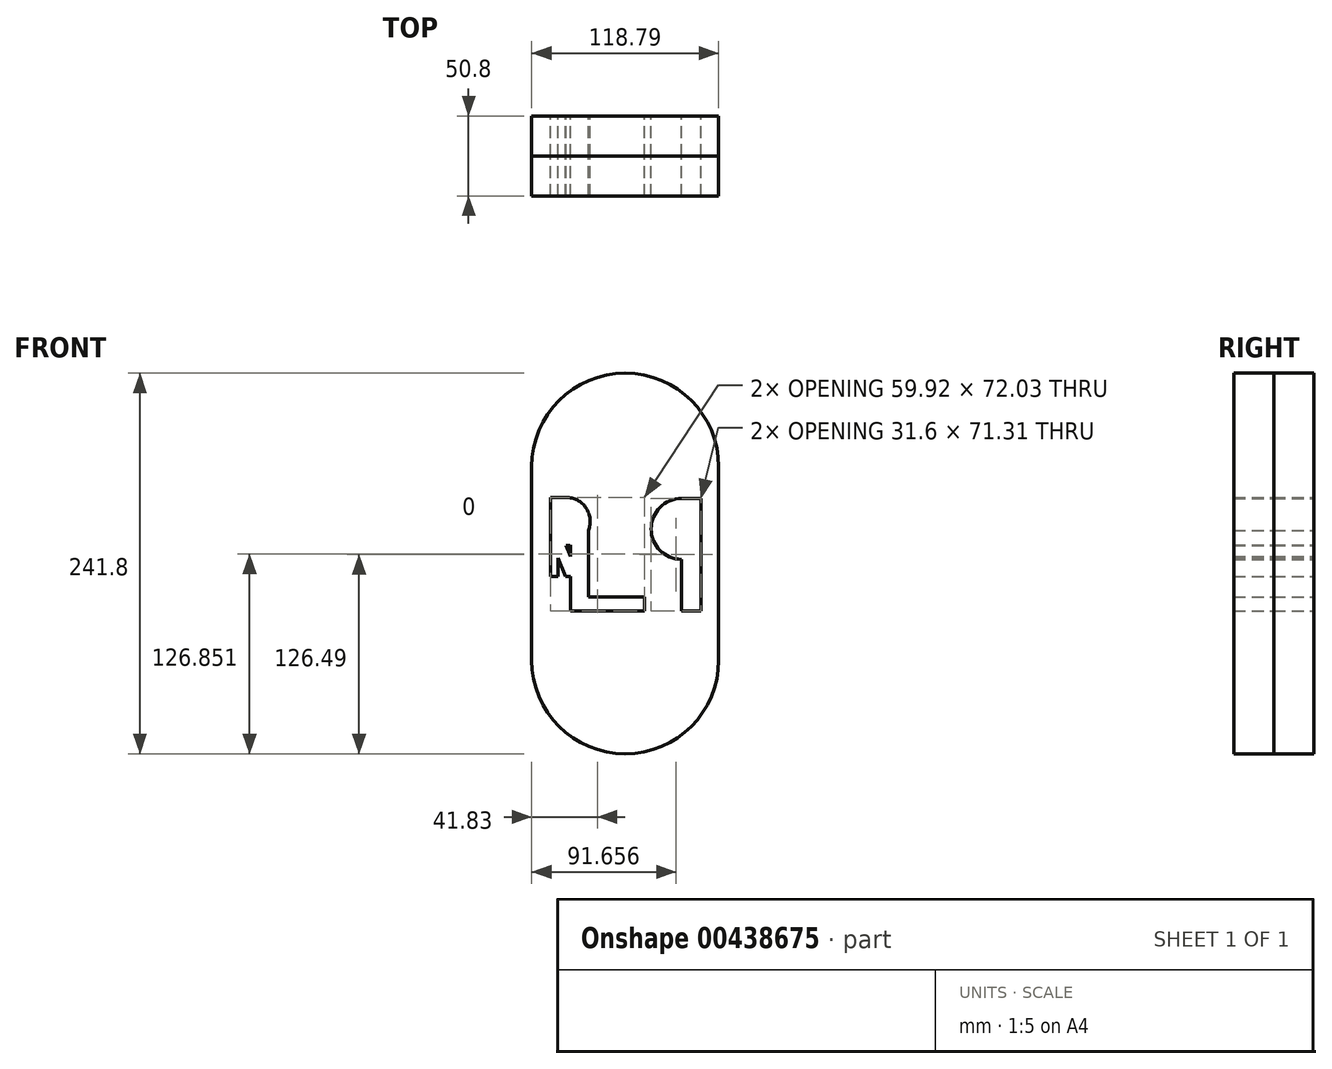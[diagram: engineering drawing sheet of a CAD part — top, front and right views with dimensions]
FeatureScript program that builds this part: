
annotation { "Feature Type Name" : "Feature", "Feature Type Description" : "" }
export const myFeature = defineFeature(function(context is Context, id is Id, definition is map)
    precondition{}
    {
        {
            var Q0;
            Q0=qCreatedBy(makeId("Front.planeOp"),FACE);
            var sketch = newSketch(context, id + "F0", { "sketchPlane" : qUnion([Q0])});
            skLineSegment(sketch, "E0", {"start": v(-56.88, 19.5) * mm, "end": v(-49.03, 0) * mm});
            skLineSegment(sketch, "E1", {"start": v(-49.03, 0) * mm, "end": v(-57.23, 0) * mm});
            skLineSegment(sketch, "E2", {"start": v(-57.23, 0) * mm, "end": v(-61.98, 11.8) * mm});
            skLineSegment(sketch, "E3", {"start": v(-61.98, 11.8) * mm, "end": v(-61.98, 0) * mm});
            skLineSegment(sketch, "E4", {"start": v(-61.98, 0) * mm, "end": v(-66.87, 0) * mm});
            skLineSegment(sketch, "E5", {"start": v(-66.87, 0) * mm, "end": v(-66.87, 50.14) * mm});
            skLineSegment(sketch, "E6", {"start": v(-66.87, 50.14) * mm, "end": v(-56.88, 50.14) * mm});
            skPoint(sketch, "E7.end.orphan", {"position": v(-66.87, 55.65) * mm});
            skPoint(sketch, "E7.start.orphan", {"position": v(-56.88, 55.65) * mm});
            skLineSegment(sketch, "E8", {"start": v(-54.12, 34.82) * mm, "end": v(-54.12, -21.9) * mm});
            skLineSegment(sketch, "E9", {"start": v(-54.12, -21.9) * mm, "end": v(-6.95, -21.9) * mm});
            skLineSegment(sketch, "E10", {"start": v(-6.95, -21.9) * mm, "end": v(-6.95, -12.97) * mm});
            skLineSegment(sketch, "E11", {"start": v(-6.95, -12.97) * mm, "end": v(-42.66, -12.97) * mm});
            skLineSegment(sketch, "E12", {"start": v(-42.66, -12.97) * mm, "end": v(-42.66, 34.82) * mm});
            skLineSegment(sketch, "E13", {"start": v(-42.66, 34.82) * mm, "end": v(-54.12, 34.82) * mm});
            skArc(sketch, "E14", {"start": v(-56.88, 19.5) * mm, "mid": v(-41.56, 34.82) * mm, "end": v(-56.88, 50.14) * mm});
            skLineSegment(sketch, "E15.bottom", {"start": v(16.44, 49.42) * mm, "end": v(28.72, 49.42) * mm});
            skLineSegment(sketch, "E15.top", {"start": v(16.44, -21.9) * mm, "end": v(28.72, -21.9) * mm});
            skLineSegment(sketch, "E15.left", {"start": v(16.44, 10.77) * mm, "end": v(16.44, -21.9) * mm});
            skLineSegment(sketch, "E15.right", {"start": v(28.72, 49.42) * mm, "end": v(28.72, -21.9) * mm});
            skPoint(sketch, "E16.end.orphan", {"position": v(0, 10.77) * mm});
            skArc(sketch, "E17", {"start": v(16.44, 49.42) * mm, "mid": v(-2.89, 30.1) * mm, "end": v(16.44, 10.77) * mm});
            skLineSegment(sketch, "E18.left", {"start": v(-78.74, 69.68) * mm, "end": v(-78.74, -53.33) * mm});
            skLineSegment(sketch, "E18.right", {"start": v(40.05, 69.68) * mm, "end": v(40.05, -53.33) * mm});
            skArc(sketch, "E19", {"start": v(-78.74, -53.33) * mm, "mid": v(-19.35, -112.73) * mm, "end": v(40.05, -53.33) * mm});
            skArc(sketch, "E20", {"start": v(40.05, 69.68) * mm, "mid": v(-19.35, 129.07) * mm, "end": v(-78.74, 69.68) * mm});
            skSolve(sketch);
        }
        {
            var Q0;
            Q0 = qSketchRegion(id + "F0", true);
            var Q1;
            {var subQ0=sQuery(id+"F0.wireOp",EDGE,"E14");var subQ1=sQuery(id+"F0.wireOp",EDGE,"E0");var subQ2=makeQuery(id+"F0.imprint","INTERSECT",VERTEX,{"derivedFrom":[subQ1,subQ0]});Q1=makeQuery(id+"F0.imprint","IMPRINT",FACE,{"disambiguationData":[TD([[makeQuery(id+"F0.imprint","IMPRINT",EDGE,{"disambiguationData":[TD([[subQ2,-1.0]])],"derivedFrom":subQ1}),1.0]])]});}
            extrude(context, id + "F1", {"entities" : qUnion([Q0, Q1]), "depth" : 25.4 * mm});
        }
        {
            var Q0;
            Q0=makeQuery(id+"F1.opExtrude","CAP_FACE",FACE,{"disambiguationData":[OSD([sQuery(id+"F0.wireOp",EDGE,"E1"),sQuery(id+"F0.wireOp",EDGE,"E2"),sQuery(id+"F0.wireOp",EDGE,"E3"),sQuery(id+"F0.wireOp",EDGE,"E4"),sQuery(id+"F0.wireOp",EDGE,"E5"),sQuery(id+"F0.wireOp",EDGE,"E6"),sQuery(id+"F0.wireOp",EDGE,"E8"),sQuery(id+"F0.wireOp",EDGE,"E9"),sQuery(id+"F0.wireOp",EDGE,"E10"),sQuery(id+"F0.wireOp",EDGE,"E11"),sQuery(id+"F0.wireOp",EDGE,"E12"),sQuery(id+"F0.wireOp",EDGE,"E14"),sQuery(id+"F0.wireOp",EDGE,"E15.bottom"),sQuery(id+"F0.wireOp",EDGE,"E15.top"),sQuery(id+"F0.wireOp",EDGE,"E15.left"),sQuery(id+"F0.wireOp",EDGE,"E15.right"),sQuery(id+"F0.wireOp",EDGE,"E17"),sQuery(id+"F0.wireOp",EDGE,"E18.left"),sQuery(id+"F0.wireOp",EDGE,"E18.right"),sQuery(id+"F0.wireOp",EDGE,"E19"),sQuery(id+"F0.wireOp",EDGE,"E20")])],"isStart":false});
            var Q1;
            Q1=makeQuery(id+"F1.opExtrude","CAP_FACE",FACE,{"disambiguationData":[OSD([sQuery(id+"F0.wireOp",EDGE,"E0"),sQuery(id+"F0.wireOp",EDGE,"E8"),sQuery(id+"F0.wireOp",EDGE,"E14")])],"isStart":false});
            extrude(context, id + "F2", {"entities" : qUnion([Q0, Q1]), "depth" : 25.4 * mm});
        }
    });
